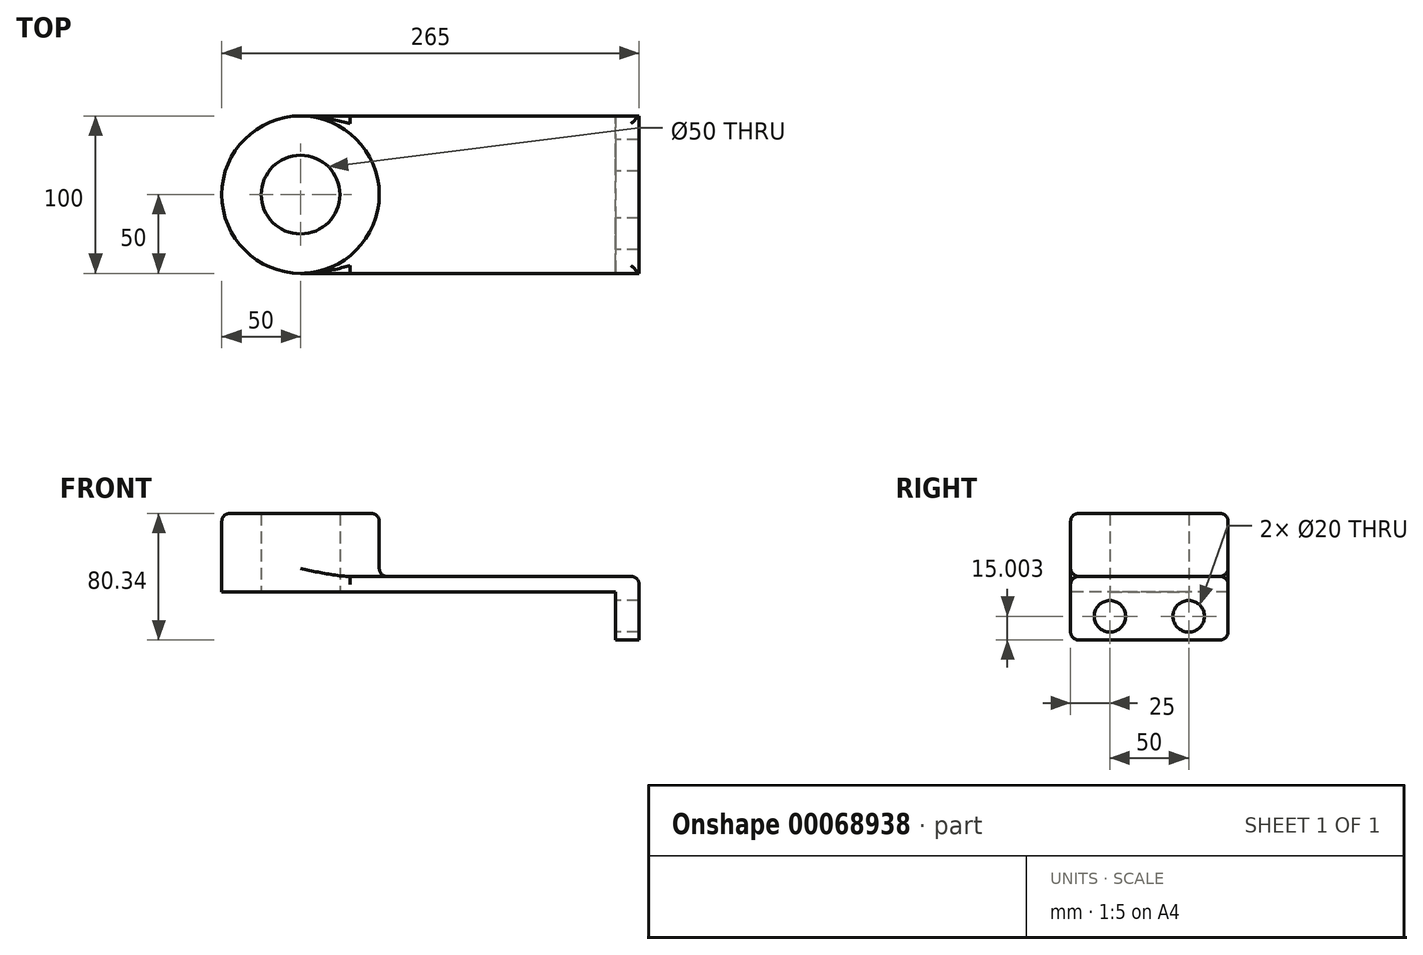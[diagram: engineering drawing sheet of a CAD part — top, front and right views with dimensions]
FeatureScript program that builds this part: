
annotation { "Feature Type Name" : "Feature", "Feature Type Description" : "" }
export const myFeature = defineFeature(function(context is Context, id is Id, definition is map)
    precondition{}
    {
        {
            var Q0;
            Q0=qCreatedBy(makeId("Top.planeOp"),FACE);
            var sketch = newSketch(context, id + "F0", { "sketchPlane" : qUnion([Q0])});
            skLineSegment(sketch, "E0.rect.bottom", {"start": v(100, 50) * mm, "end": v(-100, 50) * mm});
            skLineSegment(sketch, "E0.rect.top", {"start": v(100, -50) * mm, "end": v(-100, -50) * mm});
            skLineSegment(sketch, "E0.rect.left", {"start": v(100, 50) * mm, "end": v(100, -50) * mm});
            skLineSegment(sketch, "E0.rect.right", {"start": v(-100, 50) * mm, "end": v(-100, -50) * mm});
            skPoint(sketch, "E0.rect.middle", {"position": v(0, 0) * mm});
            skCircle(sketch, "E1", {"center": v(-100, 0) * mm, "radius": 50 * mm});
            skCircle(sketch, "E2", {"center": v(-100, 0) * mm, "radius": 25 * mm});
            skSolve(sketch);
        }
        {
            var Q0;
            Q0 = qSketchRegion(id + "F0", true);
            extrude(context, id + "F1", {"entities" : qUnion([Q0]), "depth" : 10 * mm});
        }
        {
            var Q0;
            {var subQ1=sQuery(id+"F0.wireOp",EDGE,"E0.rect.right");var subQ3=sQuery(id+"F0.wireOp",EDGE,"E2");var subQ4=makeQuery(id+"F0.imprint","INTERSECT",VERTEX,{"disambiguationData":[OD(0.0)],"derivedFrom":[subQ1,subQ3]});Q0=makeQuery(id+"F0.imprint","IMPRINT",FACE,{"disambiguationData":[TD([[makeQuery(id+"F0.imprint","IMPRINT",EDGE,{"disambiguationData":[TD([[subQ4,-1.0]])],"derivedFrom":subQ3}),-1.0]])]});}
            var Q1;
            {var subQ1=sQuery(id+"F0.wireOp",EDGE,"E0.rect.right");var subQ3=sQuery(id+"F0.wireOp",EDGE,"E2");var subQ4=makeQuery(id+"F0.imprint","INTERSECT",VERTEX,{"disambiguationData":[OD(0.0)],"derivedFrom":[subQ1,subQ3]});Q1=makeQuery(id+"F0.imprint","IMPRINT",FACE,{"disambiguationData":[TD([[makeQuery(id+"F0.imprint","IMPRINT",EDGE,{"disambiguationData":[TD([[subQ4,1.0]])],"derivedFrom":subQ3}),-1.0]])]});}
            extrude(context, id + "F2", {"entities" : qUnion([Q0, Q1]), "operationType" : NewBodyOperationType.ADD, "depth" : 25 * mm});
        }
        {
            var Q0;
            Q0=makeQuery(id+"F2.opExtrude","CAP_FACE",FACE,{"disambiguationData":[OSD([sQuery(id+"F0.wireOp",EDGE,"E1"),sQuery(id+"F0.wireOp",EDGE,"E2")])],"isStart":false});
            extrude(context, id + "F3", {"entities" : qUnion([Q0]), "operationType" : NewBodyOperationType.ADD, "depth" : 25 * mm});
        }
        {
            var Q0;
            Q0=makeQuery(id+"F1.opExtrude","SWEPT_FACE",FACE,{"disambiguationData":[OSD([sQuery(id+"F0.wireOp",EDGE,"E0.rect.left")])]});
            var sketch = newSketch(context, id + "F4", { "sketchPlane" : qUnion([Q0])});
            skPoint(sketch, "E3.oppositeSnap0", {"position": v(50, 5) * mm});
            skLineSegment(sketch, "E3.bottom", {"start": v(-50, 10) * mm, "end": v(50, 10) * mm});
            skLineSegment(sketch, "E3.top", {"start": v(-50, -30.34) * mm, "end": v(50, -30.34) * mm});
            skLineSegment(sketch, "E3.left", {"start": v(-50, 10) * mm, "end": v(-50, -30.34) * mm});
            skLineSegment(sketch, "E3.right", {"start": v(50, 10) * mm, "end": v(50, -30.34) * mm});
            skCircle(sketch, "E4", {"center": v(-25, -15.34) * mm, "radius": 10 * mm});
            skLineSegment(sketch, "E5", {"start": v(0, 0) * mm, "end": v(0, -30.34) * mm, "construction": true});
            skCircle(sketch, "E6.MirrorC", {"center": v(25, -15.34) * mm, "radius": 10 * mm});
            skSolve(sketch);
        }
        {
            var Q0;
            Q0 = qSketchRegion(id + "F4", true);
            extrude(context, id + "F5", {"entities" : qUnion([Q0]), "operationType" : NewBodyOperationType.ADD, "depth" : 15 * mm});
        }
        {
            var Q0;
            {var subQ0=sQuery(id+"F0.wireOp",EDGE,"E1");Q0=makeQuery(id+"F2.boolean.opBoolean","INTERSECT",EDGE,{"derivedFrom":[makeQuery(id+"F1.opExtrude","CAP_FACE",FACE,{"disambiguationData":[OSD([sQuery(id+"F0.wireOp",EDGE,"E0.rect.bottom"),sQuery(id+"F0.wireOp",EDGE,"E0.rect.top"),sQuery(id+"F0.wireOp",EDGE,"E0.rect.left"),subQ0,sQuery(id+"F0.wireOp",EDGE,"E2")])],"isStart":false}),makeQuery(id+"F2.opExtrude","SWEPT_FACE",FACE,{"disambiguationData":[OSD([subQ0])]})]});}
            fillet(context, id + "F6", {"entities" : qUnion([Q0]), "radius" : 5 * mm, "tangentPropagation" : true, "allowEdgeOverflow" : false});
        }
        {
            var Q0;
            Q0=makeQuery(id+"F5.opExtrude","CAP_EDGE",EDGE,{"disambiguationData":[OSD([sQuery(id+"F4.wireOp",EDGE,"E3.bottom")])],"isStart":false});
            var Q1;
            Q1=makeQuery(id+"F5.boolean.opBoolean","MERGE",EDGE,{"derivedFrom":[makeQuery(id+"F1.opExtrude","CAP_EDGE",EDGE,{"disambiguationData":[OSD([sQuery(id+"F0.wireOp",EDGE,"E0.rect.top")])],"isStart":false}),makeQuery(id+"F5.opExtrude","SWEPT_EDGE",EDGE,{"disambiguationData":[OSD([sQuery(id+"F4.wireOp",EDGE,"E3.bottom"),sQuery(id+"F4.wireOp",EDGE,"E3.left")])]})]});
            var Q2;
            Q2=makeQuery(id+"F5.boolean.opBoolean","MERGE",EDGE,{"derivedFrom":[makeQuery(id+"F1.opExtrude","CAP_EDGE",EDGE,{"disambiguationData":[OSD([sQuery(id+"F0.wireOp",EDGE,"E0.rect.bottom")])],"isStart":false}),makeQuery(id+"F5.opExtrude","SWEPT_EDGE",EDGE,{"disambiguationData":[OSD([sQuery(id+"F4.wireOp",EDGE,"E3.bottom"),sQuery(id+"F4.wireOp",EDGE,"E3.right")])]})]});
            var Q3;
            Q3=makeQuery(id+"F5.opExtrude","SWEPT_EDGE",EDGE,{"disambiguationData":[OSD([sQuery(id+"F4.wireOp",EDGE,"E3.top"),sQuery(id+"F4.wireOp",EDGE,"E3.left")])]});
            var Q4;
            Q4=makeQuery(id+"F5.opExtrude","SWEPT_EDGE",EDGE,{"disambiguationData":[OSD([sQuery(id+"F4.wireOp",EDGE,"E3.top"),sQuery(id+"F4.wireOp",EDGE,"E3.right")])]});
            var Q5;
            Q5=makeQuery(id+"F3.opExtrude","CAP_EDGE",EDGE,{"disambiguationData":[OSD([sQuery(id+"F0.wireOp",EDGE,"E1")])],"isStart":false});
            fillet(context, id + "F7", {"entities" : qUnion([Q0, Q1, Q2, Q3, Q4, Q5]), "radius" : 5 * mm, "tangentPropagation" : true, "allowEdgeOverflow" : false});
        }
    });
